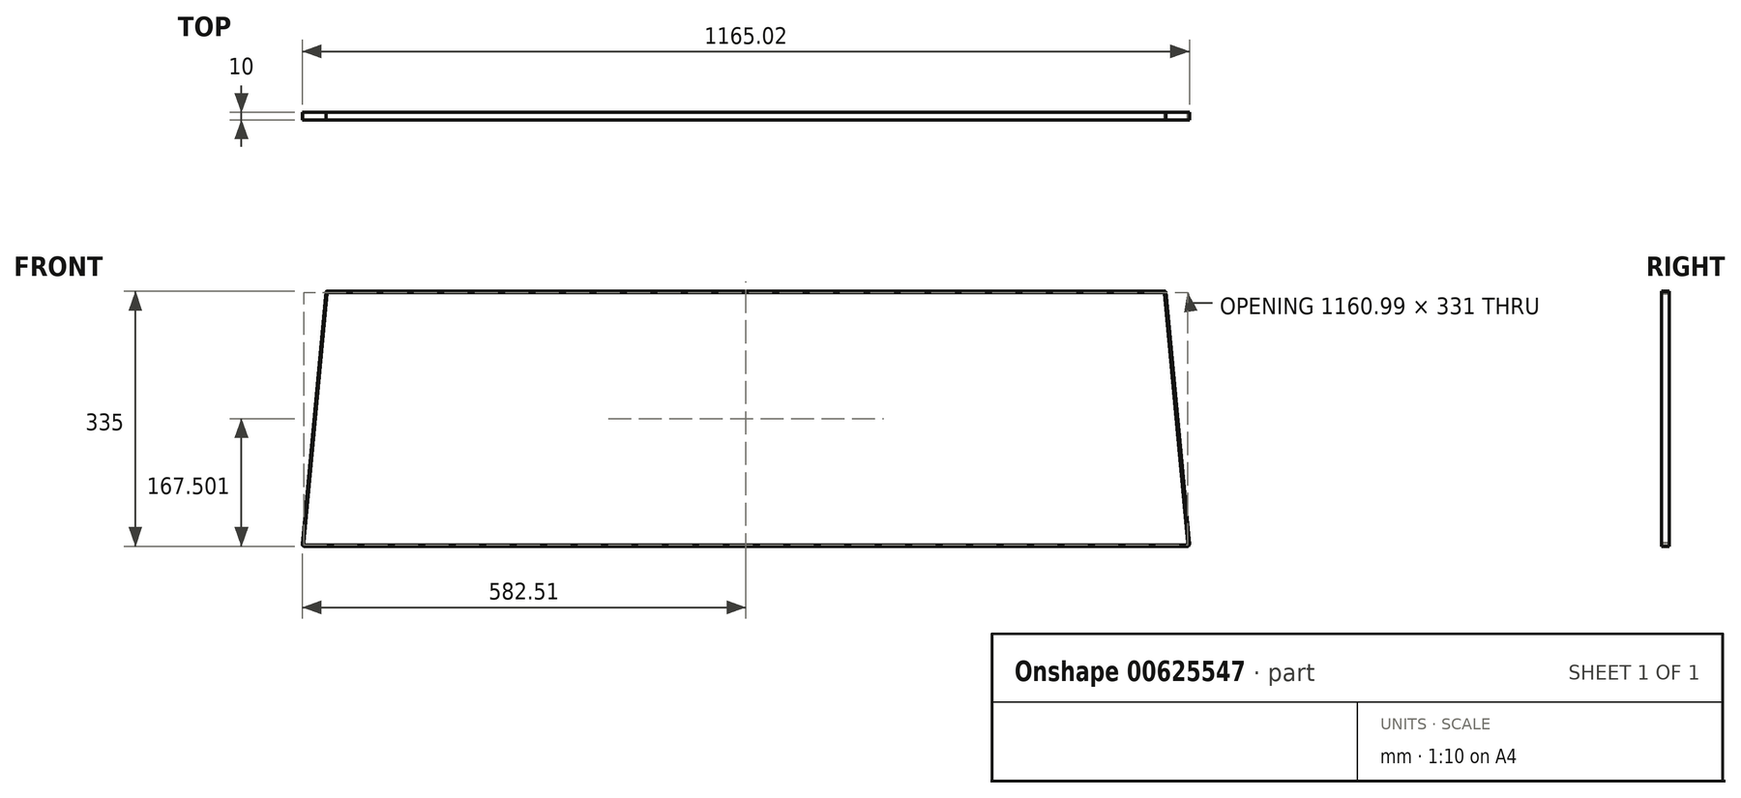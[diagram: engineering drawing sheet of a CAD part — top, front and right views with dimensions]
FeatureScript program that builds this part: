
annotation { "Feature Type Name" : "Feature", "Feature Type Description" : "" }
export const myFeature = defineFeature(function(context is Context, id is Id, definition is map)
    precondition{}
    {
        {
            var Q0;
            Q0=qCreatedBy(makeId("Front.planeOp"),FACE);
            var sketch = newSketch(context, id + "F0", { "sketchPlane" : qUnion([Q0])});
            skLineSegment(sketch, "E0.bottom", {"start": v(-550, 187.58) * mm, "end": v(0, 187.58) * mm});
            skLineSegment(sketch, "E0.top", {"start": v(-580, -147.42) * mm, "end": v(6.16, -147.42) * mm});
            skPoint(sketch, "E0.middle", {"position": v(0, 17.58) * mm});
            skLineSegment(sketch, "E1.bottom", {"start": v(-548, 185.58) * mm, "end": v(0, 185.58) * mm});
            skLineSegment(sketch, "E1.top", {"start": v(-578, -145.42) * mm, "end": v(0, -145.42) * mm});
            skArc(sketch, "E2.filletArc", {"start": v(-548, 185.58) * mm, "mid": v(-549.01, 185.37) * mm, "end": v(-549.85, 184.76) * mm});
            skArc(sketch, "E3.filletArc", {"start": v(-550, 187.58) * mm, "mid": v(-550.8, 187.45) * mm, "end": v(-551.5, 187.08) * mm});
            skArc(sketch, "E4.filletArc", {"start": v(-580.5, -142.77) * mm, "mid": v(-579.82, -144.63) * mm, "end": v(-578, -145.42) * mm});
            skArc(sketch, "E5.filletArc", {"start": v(-582.5, -144.66) * mm, "mid": v(-581.86, -146.6) * mm, "end": v(-580, -147.42) * mm});
            skLineSegment(sketch, "E6", {"start": v(-551.5, 187.08) * mm, "end": v(-582.5, -144.66) * mm});
            skLineSegment(sketch, "E7", {"start": v(0, 17.58) * mm, "end": v(0, 395.2) * mm, "construction": true});
            skPoint(sketch, "E7.endSnap0", {"position": v(0, 182.6) * mm});
            skLineSegment(sketch, "E8", {"start": v(-549.85, 184.76) * mm, "end": v(-580.5, -142.77) * mm});
            skArc(sketch, "E9.MirrorCS", {"start": v(548, 185.58) * mm, "mid": v(549.01, 185.37) * mm, "end": v(549.85, 184.76) * mm});
            skArc(sketch, "E10.MirrorCS", {"start": v(580.5, -142.77) * mm, "mid": v(579.82, -144.63) * mm, "end": v(578, -145.42) * mm});
            skArc(sketch, "E11.MirrorCS", {"start": v(550, 187.58) * mm, "mid": v(550.8, 187.45) * mm, "end": v(551.5, 187.08) * mm});
            skArc(sketch, "E12.MirrorCS", {"start": v(582.5, -144.66) * mm, "mid": v(581.86, -146.6) * mm, "end": v(580, -147.42) * mm});
            skLineSegment(sketch, "E13.MirrorCS", {"start": v(580, -147.42) * mm, "end": v(-6.16, -147.42) * mm});
            skLineSegment(sketch, "E14.MirrorCS", {"start": v(549.85, 184.76) * mm, "end": v(580.5, -142.77) * mm});
            skLineSegment(sketch, "E15.MirrorCS", {"start": v(548, 185.58) * mm, "end": v(0, 185.58) * mm});
            skLineSegment(sketch, "E16.MirrorCS", {"start": v(578, -145.42) * mm, "end": v(0, -145.42) * mm});
            skLineSegment(sketch, "E17.MirrorCS", {"start": v(550, 187.58) * mm, "end": v(0, 187.58) * mm});
            skLineSegment(sketch, "E18.MirrorCS", {"start": v(551.5, 187.08) * mm, "end": v(582.5, -144.66) * mm});
            skSolve(sketch);
        }
        {
            var Q0;
            Q0=makeQuery(id+"F0.imprint","IMPRINT",FACE,{"disambiguationData":[TD([[makeQuery(id+"F0.imprint","IMPRINT",EDGE,{"derivedFrom":sQuery(id+"F0.wireOp",EDGE,"E0.bottom")}),-1.0]])]});
            extrude(context, id + "F1", {"entities" : qUnion([Q0]), "depth" : 10 * mm, "offsetDistance" : 25 * mm});
        }
    });
